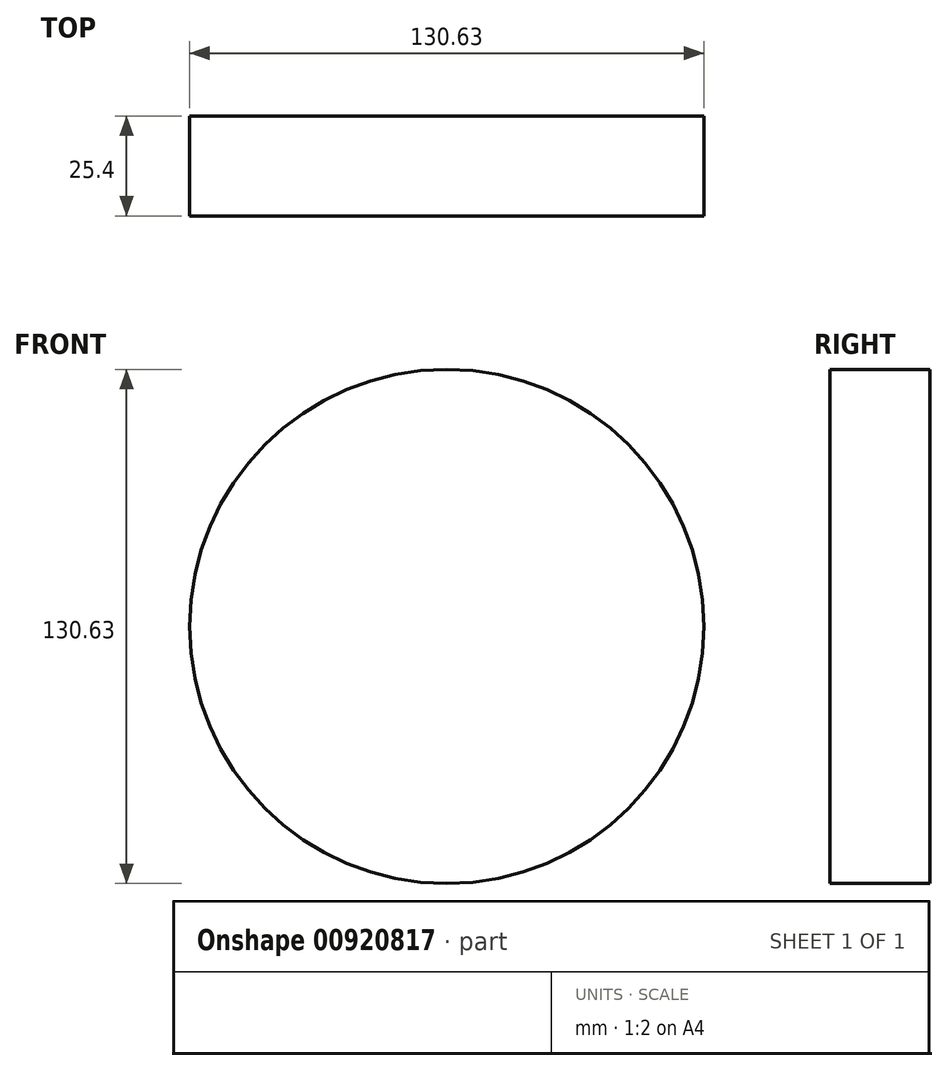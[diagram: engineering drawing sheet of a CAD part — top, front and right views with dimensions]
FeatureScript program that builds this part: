
annotation { "Feature Type Name" : "Feature", "Feature Type Description" : "" }
export const myFeature = defineFeature(function(context is Context, id is Id, definition is map)
    precondition{}
    {
        {
            var Q0;
            Q0=qCreatedBy(makeId("Front.planeOp"),FACE);
            var sketch = newSketch(context, id + "F0", { "sketchPlane" : qUnion([Q0])});
            skCircle(sketch, "E0", {"center": v(52.85, 19.04) * mm, "radius": 65.32 * mm});
            skSolve(sketch);
        }
        {
            var Q0;
            Q0=sQuery(id+"F0.wireOp",EDGE,"E0");
            extrude(context, id + "F1", {"bodyType" : ToolBodyType.SURFACE, "surfaceEntities" : qUnion([Q0]), "depth" : 25.4 * mm, "offsetDistance" : 25.4 * mm});
        }
    });
